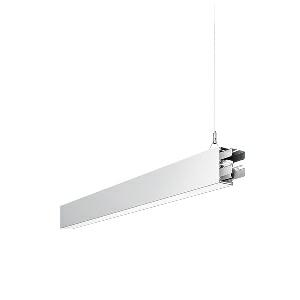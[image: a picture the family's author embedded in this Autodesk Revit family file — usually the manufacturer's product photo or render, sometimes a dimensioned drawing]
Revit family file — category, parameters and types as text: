
# Revit family: idoo_line_-_ilp_3000_830_d_mid_00805723_ae45
name_source: partatom
category: Lighting Fixtures
units: mm (PartAtom-declared; Revit-internal decimal feet)

## family parameters
Cut with Voids When Loaded = No
Host = Face
Light Source = No
Part Type = Normal
Room Calculation Point = No
Round Connector Dimension = Use Diameter
Shared = No

## types (1)
- IDOO.line - ILP 3000/830/D MID (1 x LED, 3000 lm, 3000K)
    Apparent Load = 23 VA
    Approval mark = CE
    CIE Flux Codes = 66 91 98 40 100
    Color Rendering = 80-89
    Color Temperature = 3000K
    Control Gear = Electronic ballast
    Default Elevation = 1800 mm
    Description = ILP 3000/830/D|Suspended luminaire|light source: LED|connected load: 220-240 V, 50/60 Hz|Power consumption: approx. 23 W|standby: approx. 0,20|luminous flux: 3000 lm|luminous efficacy: 130 lm/W|light distribution: Direct/indirect|direct ratio: approx. 40 %|colour temperature: Warm white, ca. 3000 K|color rendering index (CRI): >= 80|chromaticity tolerance:  3 SDCM|System of protection: IP 40|technology: Continuously dimmable|luminaire body|material: Sectional aluminium|colour: White|lamp cover: Acrylic (PMMA), Clear|mains lead: 1,0 m With free stranded wires|Fastening: Steel cable 0.3 - 0.7 m|glare control: Prism aperture|luminance(L65): <= 2700 cd/m|unified glare rating(4H 8H): <=  16|special features: DALI Load 1x, TouchDIM - dimming via standard switch, Through-wired, up to 18 m on one mains connection, Flicker-free, Suitable as emergency lighting, Mechanical and electrical connection of the individual modules without tools|
    Frequency = 50 Hz
    Height = 110 mm
    Lamp = 1 x LED
    Lamp Light Flux = 3000 lm
    Lamp count = 1
    Length = 1122 mm
    Luminous efficacy = 130 lm/W
    Manufacturer = Waldmann
    ModVariant = No
    Model = 00805723
    Mounting Place = Ceiling
    Mounting Type = Pendant
    Number of Poles = 1
    OnlyDefault = Yes
    Power Factor = 1
    Product Name = IDOO.line - ILP 3000/830/D MID
    Product group = Suspended luminaire
    ProductGroupID = 9
    Protection Class = Protection class I
    Protection Degree = IP 40
    RLX_Detail_Level = 1
    RLX_Emergency_Light_Flux = 0 lm
    RLX_Emergency_Type = 0
    RLX_Emergency_Type_DB = No
    RlxData = <blob elided: 19293 chars, md5=c9cdf41d>
    Socket = socket
    Standby Power = 0 W
    System Light Flux = 3000 lm
    System Power = 23 W
    Type Comments = Product without accessories
    Type Image = 113302000-00692570.jpg
    URL = http://relux.com
    VarID = ---
    Voltage = 230 V
    Voltage Range = 220-240 V
    Weight = 0.00 kg
    Width = 60 mm  [stored 0.19685 ft]

note: [stored X ft] marks values corroborated as IEEE doubles in the binary element streams (Revit-internal decimal feet)

## geometry (parser evidence)
native form markers: Blend x4, Sweep x14
no freeform markers — native parametric forms only
